# Revit family: NS-T7070（400,600,800）（多用途I型てすり）
name_source: partatom
category: 一般モデル
revit_build: Autodesk Revit 2015 (Build: 20140606_1530(x64)
units: mm (PartAtom-declared; Revit-internal decimal feet)

## types (6) — shared parameters
D1 = 100  [stored 0.328084 ft]
N_D1 = 100  [stored 0.328084 ft]
N_仕様① = ●手すり本体（笠木φ34）　表面材：半硬質樹脂（抗菌剤入り）+軟質樹脂二層成形　芯材：ステンレス鋼管φ27.2x1.5t（木目調色はウッドパウダーを混合）　●ブラケットカバー　樹脂成形品・笠木同色仕上　●固定座金　ステンレス
N_品名 = 補助手すり　愛の手NS
N_手すり径 = 34
N_製造元 = ナカ工業株式会社

## per-type parameters (varying)
| type | BKカバー | N_L1 | N_形式① | 笠木色1 | 笠木色2 | 笠木色R1 | 笠木色R2 |
| NS-T400 | 笠木No.00ホワイト | 400  [stored 1.31234 ft] | NS-T400 | 笠木No.00ホワイト | 笠木No.00ホワイト | 笠木No.00ホワイト | 笠木No.00ホワイト |
| NS-T600 | 笠木No.00ホワイト | 600 | NS-T600 | 笠木No.00ホワイト | 笠木No.00ホワイト | 笠木No.00ホワイト | 笠木No.00ホワイト |
| NS-T800 | 笠木No.00ホワイト | 800 | NS-T800 | 笠木No.00ホワイト | 笠木No.00ホワイト | 笠木No.00ホワイト | 笠木No.00ホワイト |
| NS-T400-M | 笠木No.73バーチ BKcover | 400  [stored 1.31234 ft] | NS-T400 | 笠木No.73バーチ(1) | 笠木No.73バーチ(2) | 笠木No.73バーチ(R1) | 笠木No.73バーチ(R2) |
| NS-T600-M | 笠木No.73バーチ BKcover | 600 | NS-T600 | 笠木No.73バーチ(1) | 笠木No.73バーチ(2) | 笠木No.73バーチ(R1) | 笠木No.73バーチ(R2) |
| NS-T800-M | 笠木No.73バーチ BKcover | 800 | NS-T800 | 笠木No.73バーチ(1) | 笠木No.73バーチ(2) | 笠木No.73バーチ(R1) | 笠木No.73バーチ(R2) |

note: [stored X ft] marks values corroborated as IEEE doubles in the binary element streams (Revit-internal decimal feet)
